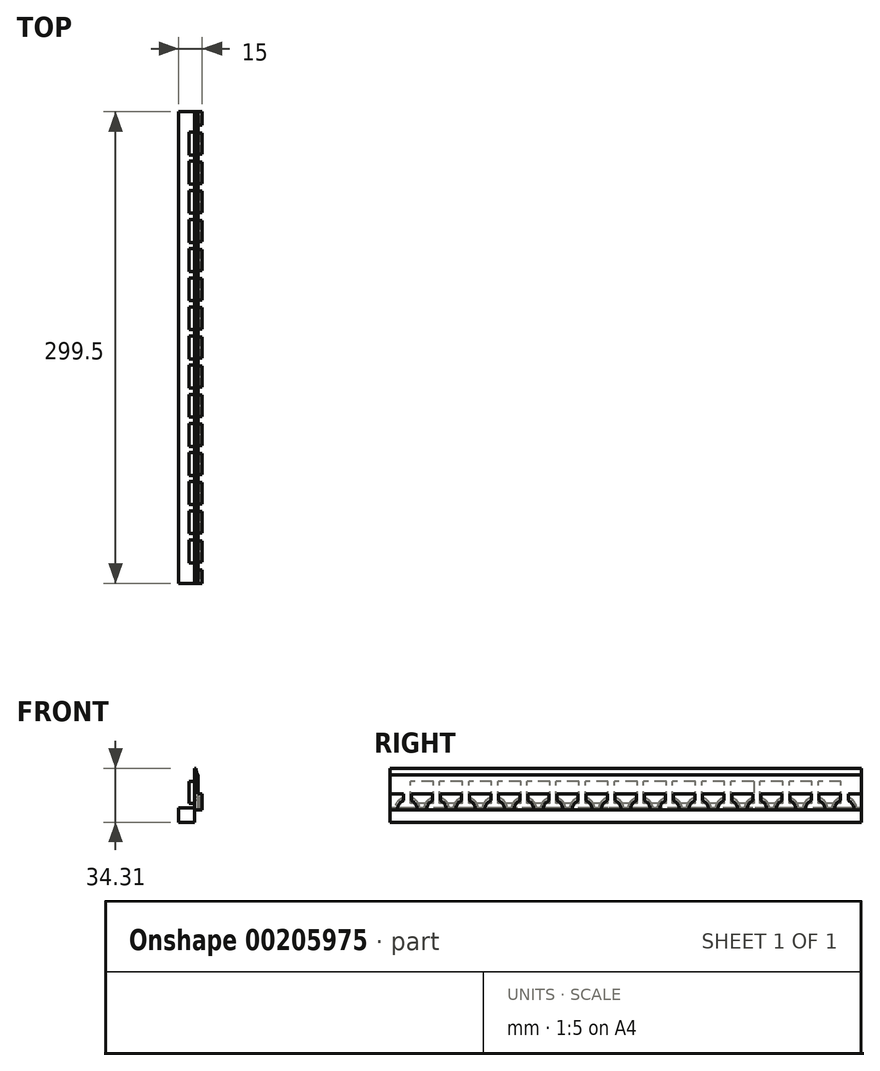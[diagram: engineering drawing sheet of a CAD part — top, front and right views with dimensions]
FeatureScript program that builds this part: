
annotation { "Feature Type Name" : "Feature", "Feature Type Description" : "" }
export const myFeature = defineFeature(function(context is Context, id is Id, definition is map)
    precondition{}
    {
        {
            var Q0;
            Q0=qCreatedBy(makeId("Front.planeOp"),FACE);
            var sketch = newSketch(context, id + "F0", { "sketchPlane" : qUnion([Q0])});
            skLineSegment(sketch, "E0.left", {"start": v(0, -1.35) * mm, "end": v(0, -9) * mm});
            skLineSegment(sketch, "E0.right", {"start": v(-10, 0) * mm, "end": v(-10, -9) * mm});
            skLineSegment(sketch, "E1.left", {"start": v(0, 1) * mm, "end": v(0, 4) * mm});
            skLineSegment(sketch, "E2", {"start": v(0, 21) * mm, "end": v(0, 25.3) * mm});
            skLineSegment(sketch, "E3", {"start": v(2.3, 21) * mm, "end": v(2.3, 10) * mm});
            skLineSegment(sketch, "E4", {"start": v(-10, -9) * mm, "end": v(0, -9) * mm});
            skLineSegment(sketch, "E5", {"start": v(0, 21) * mm, "end": v(0, 4) * mm});
            skLineSegment(sketch, "E6", {"start": v(2.3, 10) * mm, "end": v(2.3, 0) * mm});
            skLineSegment(sketch, "E7", {"start": v(2.3, 0) * mm, "end": v(2.3, -1) * mm});
            skLineSegment(sketch, "E8", {"start": v(-10, 0) * mm, "end": v(0, 0) * mm});
            skLineSegment(sketch, "E9", {"start": v(0, 25.3) * mm, "end": v(1, 25.3) * mm});
            skFitSpline(sketch, "E10", {"points": [v(1, 25.3) * mm, v(2.3, 21) * mm, v(6.9, 18.23) * mm], "startDerivative": vector(1.27, -9.9) * mm, "endDerivative": vector(10.4, -4.34) * mm});
            skPoint(sketch, "E11.0.internal.orphan", {"position": v(1, 26) * mm});
            skLineSegment(sketch, "E12", {"start": v(0, 0) * mm, "end": v(0, 1) * mm});
            skLineSegment(sketch, "E13", {"start": v(0, 0) * mm, "end": v(0, -1) * mm});
            skLineSegment(sketch, "E14", {"start": v(0, -1) * mm, "end": v(2.3, -1) * mm});
            skLineSegment(sketch, "E15", {"start": v(0, -1) * mm, "end": v(0, -1.35) * mm});
            skPoint(sketch, "E16.orphan", {"position": v(2.3, -1.35) * mm});
            skSolve(sketch);
        }
        {
            var Q0;
            Q0=qCreatedBy(makeId("Right.planeOp"),FACE);
            var sketch = newSketch(context, id + "F1", { "sketchPlane" : qUnion([Q0])});
            skLineSegment(sketch, "E17.left", {"start": v(13, 4) * mm, "end": v(13, 17) * mm});
            skLineSegment(sketch, "E17.right", {"start": v(27.5, 4) * mm, "end": v(27.5, 17) * mm});
            skLineSegment(sketch, "E18.left", {"start": v(31.5, 4) * mm, "end": v(31.5, 17) * mm});
            skLineSegment(sketch, "E18.right", {"start": v(46, 4) * mm, "end": v(46, 17) * mm});
            skLineSegment(sketch, "E19.left", {"start": v(50, 4) * mm, "end": v(50, 17) * mm});
            skLineSegment(sketch, "E19.right", {"start": v(64.5, 4) * mm, "end": v(64.5, 17) * mm});
            skLineSegment(sketch, "E20.left", {"start": v(68.5, 4) * mm, "end": v(68.5, 17) * mm});
            skLineSegment(sketch, "E20.right", {"start": v(83, 4) * mm, "end": v(83, 17) * mm});
            skLineSegment(sketch, "E21.left", {"start": v(87, 4) * mm, "end": v(87, 17) * mm});
            skLineSegment(sketch, "E21.right", {"start": v(101.5, 4) * mm, "end": v(101.5, 17) * mm});
            skLineSegment(sketch, "E22.left", {"start": v(105.5, 4) * mm, "end": v(105.5, 17) * mm});
            skLineSegment(sketch, "E22.right", {"start": v(120, 4) * mm, "end": v(120, 17) * mm});
            skLineSegment(sketch, "E23.left", {"start": v(124, 4) * mm, "end": v(124, 17) * mm});
            skLineSegment(sketch, "E23.right", {"start": v(138.5, 4) * mm, "end": v(138.5, 17) * mm});
            skLineSegment(sketch, "E24.left", {"start": v(142.5, 4) * mm, "end": v(142.5, 17) * mm});
            skLineSegment(sketch, "E24.right", {"start": v(157, 4) * mm, "end": v(157, 17) * mm});
            skLineSegment(sketch, "E25.left", {"start": v(161, 4) * mm, "end": v(161, 17) * mm});
            skLineSegment(sketch, "E25.right", {"start": v(175.5, 4) * mm, "end": v(175.5, 17) * mm});
            skLineSegment(sketch, "E26.left", {"start": v(179.5, 4) * mm, "end": v(179.5, 17) * mm});
            skLineSegment(sketch, "E26.right", {"start": v(194, 4) * mm, "end": v(194, 17) * mm});
            skLineSegment(sketch, "E27.left", {"start": v(198, 4) * mm, "end": v(198, 17) * mm});
            skLineSegment(sketch, "E27.right", {"start": v(212.5, 4) * mm, "end": v(212.5, 17) * mm});
            skLineSegment(sketch, "E28.left", {"start": v(216.5, 4) * mm, "end": v(216.5, 17) * mm});
            skLineSegment(sketch, "E28.right", {"start": v(231, 4) * mm, "end": v(231, 17) * mm});
            skLineSegment(sketch, "E29.left", {"start": v(235, 4) * mm, "end": v(235, 17) * mm});
            skLineSegment(sketch, "E29.right", {"start": v(249.5, 4) * mm, "end": v(249.5, 17) * mm});
            skLineSegment(sketch, "E30.left", {"start": v(253.5, 4) * mm, "end": v(253.5, 17) * mm});
            skLineSegment(sketch, "E30.right", {"start": v(268, 4) * mm, "end": v(268, 17) * mm});
            skLineSegment(sketch, "E31.left", {"start": v(272, 4) * mm, "end": v(272, 17) * mm});
            skLineSegment(sketch, "E31.right", {"start": v(286.5, 4) * mm, "end": v(286.5, 17) * mm});
            skLineSegment(sketch, "E32", {"start": v(286.5, 17) * mm, "end": v(272, 17) * mm});
            skLineSegment(sketch, "E33", {"start": v(286.5, 4) * mm, "end": v(286.5, 3) * mm});
            skLineSegment(sketch, "E34", {"start": v(286.5, 3) * mm, "end": v(272, 3) * mm});
            skLineSegment(sketch, "E35", {"start": v(13, 4) * mm, "end": v(13, 3) * mm});
            skLineSegment(sketch, "E36", {"start": v(27.5, 4) * mm, "end": v(27.5, 3) * mm});
            skLineSegment(sketch, "E37", {"start": v(31.5, 4) * mm, "end": v(31.5, 3) * mm});
            skLineSegment(sketch, "E38", {"start": v(46, 4) * mm, "end": v(46, 3) * mm});
            skLineSegment(sketch, "E39", {"start": v(50, 4) * mm, "end": v(50, 3) * mm});
            skLineSegment(sketch, "E40", {"start": v(64.5, 4) * mm, "end": v(64.5, 3) * mm});
            skLineSegment(sketch, "E41", {"start": v(68.5, 4) * mm, "end": v(68.5, 3) * mm});
            skLineSegment(sketch, "E42", {"start": v(83, 4) * mm, "end": v(83, 3) * mm});
            skLineSegment(sketch, "E43", {"start": v(87, 4) * mm, "end": v(87, 3) * mm});
            skLineSegment(sketch, "E44", {"start": v(101.5, 4) * mm, "end": v(101.5, 3) * mm});
            skLineSegment(sketch, "E45", {"start": v(105.5, 4) * mm, "end": v(105.5, 3) * mm});
            skLineSegment(sketch, "E46", {"start": v(120, 4) * mm, "end": v(120, 3) * mm});
            skLineSegment(sketch, "E47", {"start": v(124, 4) * mm, "end": v(124, 3) * mm});
            skLineSegment(sketch, "E48", {"start": v(138.5, 4) * mm, "end": v(138.5, 3) * mm});
            skLineSegment(sketch, "E49", {"start": v(142.5, 4) * mm, "end": v(142.5, 3) * mm});
            skLineSegment(sketch, "E50", {"start": v(157, 4) * mm, "end": v(157, 3) * mm});
            skLineSegment(sketch, "E51", {"start": v(161, 4) * mm, "end": v(161, 3) * mm});
            skLineSegment(sketch, "E52", {"start": v(175.5, 4) * mm, "end": v(175.5, 3) * mm});
            skLineSegment(sketch, "E53", {"start": v(179.5, 4) * mm, "end": v(179.5, 3) * mm});
            skLineSegment(sketch, "E54", {"start": v(194, 4) * mm, "end": v(194, 3) * mm});
            skLineSegment(sketch, "E55", {"start": v(198, 4) * mm, "end": v(198, 3) * mm});
            skLineSegment(sketch, "E56", {"start": v(212.5, 4) * mm, "end": v(212.5, 3) * mm});
            skLineSegment(sketch, "E57", {"start": v(216.5, 4) * mm, "end": v(216.5, 3) * mm});
            skLineSegment(sketch, "E58", {"start": v(231, 4) * mm, "end": v(231, 3) * mm});
            skLineSegment(sketch, "E59", {"start": v(235, 4) * mm, "end": v(235, 3) * mm});
            skLineSegment(sketch, "E60", {"start": v(249.5, 4) * mm, "end": v(249.5, 3) * mm});
            skLineSegment(sketch, "E61", {"start": v(253.5, 4) * mm, "end": v(253.5, 3) * mm});
            skLineSegment(sketch, "E62", {"start": v(268, 4) * mm, "end": v(268, 3) * mm});
            skLineSegment(sketch, "E63", {"start": v(272, 4) * mm, "end": v(272, 3) * mm});
            skLineSegment(sketch, "E64.trimOffspring", {"start": v(268, 17) * mm, "end": v(253.5, 17) * mm});
            skLineSegment(sketch, "E65.trimOffspring", {"start": v(249.5, 17) * mm, "end": v(235, 17) * mm});
            skLineSegment(sketch, "E66.trimOffspring", {"start": v(268, 3) * mm, "end": v(253.5, 3) * mm});
            skLineSegment(sketch, "E67.trimOffspring", {"start": v(249.5, 3) * mm, "end": v(235, 3) * mm});
            skLineSegment(sketch, "E68.trimOffspring", {"start": v(231, 3) * mm, "end": v(216.5, 3) * mm});
            skLineSegment(sketch, "E69.trimOffspring", {"start": v(231, 17) * mm, "end": v(216.5, 17) * mm});
            skLineSegment(sketch, "E70.trimOffspring", {"start": v(212.5, 17) * mm, "end": v(198, 17) * mm});
            skLineSegment(sketch, "E71.trimOffspring", {"start": v(212.5, 3) * mm, "end": v(198, 3) * mm});
            skLineSegment(sketch, "E72.trimOffspring", {"start": v(194, 17) * mm, "end": v(179.5, 17) * mm});
            skLineSegment(sketch, "E73.trimOffspring", {"start": v(194, 3) * mm, "end": v(179.5, 3) * mm});
            skLineSegment(sketch, "E74.trimOffspring", {"start": v(175.5, 17) * mm, "end": v(161, 17) * mm});
            skLineSegment(sketch, "E75.trimOffspring", {"start": v(175.5, 3) * mm, "end": v(161, 3) * mm});
            skLineSegment(sketch, "E76.trimOffspring", {"start": v(157, 17) * mm, "end": v(142.5, 17) * mm});
            skLineSegment(sketch, "E77.trimOffspring", {"start": v(157, 3) * mm, "end": v(142.5, 3) * mm});
            skLineSegment(sketch, "E78.trimOffspring", {"start": v(138.5, 17) * mm, "end": v(124, 17) * mm});
            skLineSegment(sketch, "E79.trimOffspring", {"start": v(138.5, 3) * mm, "end": v(124, 3) * mm});
            skLineSegment(sketch, "E80.trimOffspring", {"start": v(120, 17) * mm, "end": v(105.5, 17) * mm});
            skLineSegment(sketch, "E81.trimOffspring", {"start": v(120, 3) * mm, "end": v(105.5, 3) * mm});
            skLineSegment(sketch, "E82.trimOffspring", {"start": v(101.5, 17) * mm, "end": v(87, 17) * mm});
            skLineSegment(sketch, "E83.trimOffspring", {"start": v(101.5, 3) * mm, "end": v(87, 3) * mm});
            skLineSegment(sketch, "E84.trimOffspring", {"start": v(83, 17) * mm, "end": v(68.5, 17) * mm});
            skLineSegment(sketch, "E85.trimOffspring", {"start": v(83, 3) * mm, "end": v(68.5, 3) * mm});
            skLineSegment(sketch, "E86.trimOffspring", {"start": v(64.5, 17) * mm, "end": v(50, 17) * mm});
            skLineSegment(sketch, "E87.trimOffspring", {"start": v(64.5, 3) * mm, "end": v(50, 3) * mm});
            skLineSegment(sketch, "E88.trimOffspring", {"start": v(46, 17) * mm, "end": v(31.5, 17) * mm});
            skLineSegment(sketch, "E89.trimOffspring", {"start": v(46, 3) * mm, "end": v(31.5, 3) * mm});
            skLineSegment(sketch, "E90.trimOffspring", {"start": v(27.5, 17) * mm, "end": v(13, 17) * mm});
            skLineSegment(sketch, "E91.trimOffspring", {"start": v(27.5, 3) * mm, "end": v(13, 3) * mm});
            skPoint(sketch, "E92.orphan", {"position": v(13, 18) * mm});
            skSolve(sketch);
        }
        {
            var Q0;
            Q0=qCreatedBy(makeId("Right.planeOp"),FACE);
            var sketch = newSketch(context, id + "F2", { "sketchPlane" : qUnion([Q0])});
            skLineSegment(sketch, "E93", {"start": v(0, 0) * mm, "end": v(0, -1) * mm});
            skLineSegment(sketch, "E94.bottom", {"start": v(0, -1) * mm, "end": v(4.75, -1) * mm});
            skLineSegment(sketch, "E95.top", {"start": v(0, 9) * mm, "end": v(8.5, 9) * mm});
            skLineSegment(sketch, "E95.left", {"start": v(0, -1) * mm, "end": v(0, 9) * mm});
            skLineSegment(sketch, "E95.right", {"start": v(8.5, 4.73) * mm, "end": v(8.5, 9) * mm});
            skLineSegment(sketch, "E96.bottom", {"start": v(17.25, -1) * mm, "end": v(23.25, -1) * mm});
            skLineSegment(sketch, "E96.top", {"start": v(13.5, 9) * mm, "end": v(27, 9) * mm});
            skLineSegment(sketch, "E96.left", {"start": v(13.5, 4.73) * mm, "end": v(13.5, 9) * mm});
            skLineSegment(sketch, "E96.right", {"start": v(27, 4.73) * mm, "end": v(27, 9) * mm});
            skArc(sketch, "E97", {"start": v(19.05, -1) * mm, "mid": v(17.52, 3.73) * mm, "end": v(13.5, 6.65) * mm});
            skArc(sketch, "E98", {"start": v(17.25, -1) * mm, "mid": v(16.23, 2.42) * mm, "end": v(13.5, 4.73) * mm});
            skLineSegment(sketch, "E99", {"start": v(35.75, -1) * mm, "end": v(41.75, -1) * mm});
            skLineSegment(sketch, "E100", {"start": v(54.25, -1) * mm, "end": v(60.25, -1) * mm});
            skLineSegment(sketch, "E101", {"start": v(72.75, -1) * mm, "end": v(78.75, -1) * mm});
            skLineSegment(sketch, "E102", {"start": v(91.25, -1) * mm, "end": v(97.25, -1) * mm});
            skLineSegment(sketch, "E103", {"start": v(109.75, -1) * mm, "end": v(115.75, -1) * mm});
            skLineSegment(sketch, "E104", {"start": v(130.1, -1) * mm, "end": v(134.25, -1) * mm});
            skLineSegment(sketch, "E105", {"start": v(146.75, -1) * mm, "end": v(152.75, -1) * mm});
            skLineSegment(sketch, "E106", {"start": v(165.25, -1) * mm, "end": v(169.4, -1) * mm});
            skLineSegment(sketch, "E107", {"start": v(180, -1) * mm, "end": v(189.75, -1) * mm});
            skLineSegment(sketch, "E108", {"start": v(202.25, -1) * mm, "end": v(208.25, -1) * mm});
            skLineSegment(sketch, "E109", {"start": v(222.6, -1) * mm, "end": v(226.75, -1) * mm});
            skLineSegment(sketch, "E110", {"start": v(239.25, -1) * mm, "end": v(245.25, -1) * mm});
            skLineSegment(sketch, "E111", {"start": v(257.75, -1) * mm, "end": v(263.75, -1) * mm});
            skPoint(sketch, "E112.endSnap0", {"position": v(168.25, -1) * mm});
            skLineSegment(sketch, "E113", {"start": v(276.25, -1) * mm, "end": v(282.25, -1) * mm});
            skLineSegment(sketch, "E114", {"start": v(294.75, -1) * mm, "end": v(299.5, -1) * mm});
            skArc(sketch, "E115", {"start": v(286, 6.7) * mm, "mid": v(281.95, 3.76) * mm, "end": v(280.4, -1) * mm});
            skArc(sketch, "E116", {"start": v(294.75, -1) * mm, "mid": v(293.73, 2.42) * mm, "end": v(291, 4.72) * mm});
            skArc(sketch, "E117", {"start": v(278.1, -1) * mm, "mid": v(276.55, 3.76) * mm, "end": v(272.5, 6.7) * mm});
            skArc(sketch, "E118", {"start": v(276.25, -1) * mm, "mid": v(275.23, 2.42) * mm, "end": v(272.5, 4.72) * mm});
            skArc(sketch, "E119", {"start": v(259.6, -1) * mm, "mid": v(258.05, 3.76) * mm, "end": v(254, 6.7) * mm});
            skArc(sketch, "E120", {"start": v(257.75, -1) * mm, "mid": v(256.73, 2.42) * mm, "end": v(254, 4.72) * mm});
            skArc(sketch, "E121", {"start": v(241.1, -1) * mm, "mid": v(239.55, 3.76) * mm, "end": v(235.5, 6.7) * mm});
            skArc(sketch, "E122", {"start": v(239.25, -1) * mm, "mid": v(238.23, 2.42) * mm, "end": v(235.5, 4.72) * mm});
            skArc(sketch, "E123", {"start": v(222.6, -1) * mm, "mid": v(221.05, 3.76) * mm, "end": v(217, 6.7) * mm});
            skArc(sketch, "E124", {"start": v(220.75, -1) * mm, "mid": v(219.73, 2.42) * mm, "end": v(217, 4.72) * mm});
            skArc(sketch, "E125", {"start": v(204.1, -1) * mm, "mid": v(202.55, 3.76) * mm, "end": v(198.5, 6.7) * mm});
            skArc(sketch, "E126", {"start": v(202.25, -1) * mm, "mid": v(201.23, 2.42) * mm, "end": v(198.5, 4.72) * mm});
            skArc(sketch, "E127", {"start": v(185.6, -1) * mm, "mid": v(184.05, 3.76) * mm, "end": v(180, 6.7) * mm});
            skArc(sketch, "E128", {"start": v(183.75, -1) * mm, "mid": v(182.73, 2.42) * mm, "end": v(180, 4.72) * mm});
            skArc(sketch, "E129", {"start": v(167.1, -1) * mm, "mid": v(165.55, 3.76) * mm, "end": v(161.5, 6.7) * mm});
            skArc(sketch, "E130", {"start": v(165.25, -1) * mm, "mid": v(164.23, 2.42) * mm, "end": v(161.5, 4.72) * mm});
            skArc(sketch, "E131", {"start": v(148.6, -1) * mm, "mid": v(147.05, 3.76) * mm, "end": v(143, 6.7) * mm});
            skArc(sketch, "E132", {"start": v(146.75, -1) * mm, "mid": v(145.73, 2.42) * mm, "end": v(143, 4.72) * mm});
            skArc(sketch, "E133", {"start": v(130.1, -1) * mm, "mid": v(128.55, 3.76) * mm, "end": v(124.5, 6.7) * mm});
            skArc(sketch, "E134", {"start": v(128.25, -1) * mm, "mid": v(127.23, 2.42) * mm, "end": v(124.5, 4.72) * mm});
            skArc(sketch, "E135", {"start": v(111.6, -1) * mm, "mid": v(110.05, 3.76) * mm, "end": v(106, 6.7) * mm});
            skArc(sketch, "E136", {"start": v(109.75, -1) * mm, "mid": v(108.73, 2.42) * mm, "end": v(106, 4.72) * mm});
            skArc(sketch, "E137", {"start": v(93.1, -1) * mm, "mid": v(91.55, 3.76) * mm, "end": v(87.5, 6.7) * mm});
            skArc(sketch, "E138", {"start": v(91.25, -1) * mm, "mid": v(90.23, 2.42) * mm, "end": v(87.5, 4.73) * mm});
            skArc(sketch, "E139", {"start": v(74.6, -1) * mm, "mid": v(73.05, 3.76) * mm, "end": v(69, 6.7) * mm});
            skArc(sketch, "E140", {"start": v(72.75, -1) * mm, "mid": v(71.73, 2.42) * mm, "end": v(69, 4.73) * mm});
            skArc(sketch, "E141", {"start": v(56.1, -1) * mm, "mid": v(54.55, 3.76) * mm, "end": v(50.5, 6.7) * mm});
            skArc(sketch, "E142", {"start": v(54.25, -1) * mm, "mid": v(53.23, 2.42) * mm, "end": v(50.5, 4.73) * mm});
            skArc(sketch, "E143", {"start": v(37.6, -1) * mm, "mid": v(36.05, 3.76) * mm, "end": v(32, 6.7) * mm});
            skArc(sketch, "E144", {"start": v(35.75, -1) * mm, "mid": v(34.73, 2.42) * mm, "end": v(32, 4.73) * mm});
            skLineSegment(sketch, "E145.top", {"start": v(32, 9) * mm, "end": v(45.5, 9) * mm});
            skLineSegment(sketch, "E145.left", {"start": v(32, 4.73) * mm, "end": v(32, 9) * mm});
            skLineSegment(sketch, "E145.right", {"start": v(45.5, 4.73) * mm, "end": v(45.5, 9) * mm});
            skLineSegment(sketch, "E146.bottom", {"start": v(60.25, -1) * mm, "end": v(54.25, -1) * mm});
            skLineSegment(sketch, "E146.top", {"start": v(64, 9) * mm, "end": v(50.5, 9) * mm});
            skLineSegment(sketch, "E146.left", {"start": v(64, 4.73) * mm, "end": v(64, 9) * mm});
            skLineSegment(sketch, "E146.right", {"start": v(50.5, 4.73) * mm, "end": v(50.5, 9) * mm});
            skLineSegment(sketch, "E147.bottom", {"start": v(72.75, -1) * mm, "end": v(76.9, -1) * mm});
            skLineSegment(sketch, "E147.top", {"start": v(69, 9) * mm, "end": v(82.5, 9) * mm});
            skLineSegment(sketch, "E147.left", {"start": v(69, 4.73) * mm, "end": v(69, 9) * mm});
            skLineSegment(sketch, "E147.right", {"start": v(82.5, 4.73) * mm, "end": v(82.5, 9) * mm});
            skLineSegment(sketch, "E148.bottom", {"start": v(93.1, -1) * mm, "end": v(95.4, -1) * mm});
            skLineSegment(sketch, "E148.top", {"start": v(87.5, 9) * mm, "end": v(101, 9) * mm});
            skLineSegment(sketch, "E148.left", {"start": v(87.5, 4.73) * mm, "end": v(87.5, 9) * mm});
            skLineSegment(sketch, "E148.right", {"start": v(101, 4.72) * mm, "end": v(101, 9) * mm});
            skLineSegment(sketch, "E149.top", {"start": v(106, 9) * mm, "end": v(119.5, 9) * mm});
            skLineSegment(sketch, "E149.left", {"start": v(106, 4.72) * mm, "end": v(106, 9) * mm});
            skLineSegment(sketch, "E149.right", {"start": v(119.5, 4.72) * mm, "end": v(119.5, 9) * mm});
            skLineSegment(sketch, "E150.bottom", {"start": v(128.25, -1) * mm, "end": v(134.25, -1) * mm});
            skLineSegment(sketch, "E150.top", {"start": v(124.5, 9) * mm, "end": v(138, 9) * mm});
            skLineSegment(sketch, "E150.left", {"start": v(124.5, 4.72) * mm, "end": v(124.5, 9) * mm});
            skLineSegment(sketch, "E150.right", {"start": v(138, 4.72) * mm, "end": v(138, 9) * mm});
            skLineSegment(sketch, "E151.top", {"start": v(143, 9) * mm, "end": v(156.5, 9) * mm});
            skLineSegment(sketch, "E151.left", {"start": v(143, 4.72) * mm, "end": v(143, 9) * mm});
            skLineSegment(sketch, "E151.right", {"start": v(156.5, 4.72) * mm, "end": v(156.5, 9) * mm});
            skLineSegment(sketch, "E152.bottom", {"start": v(165.25, -1) * mm, "end": v(171.25, -1) * mm});
            skLineSegment(sketch, "E152.top", {"start": v(161.5, 9) * mm, "end": v(175, 9) * mm});
            skLineSegment(sketch, "E152.left", {"start": v(161.5, 4.72) * mm, "end": v(161.5, 9) * mm});
            skLineSegment(sketch, "E152.right", {"start": v(175, 4.72) * mm, "end": v(175, 9) * mm});
            skLineSegment(sketch, "E153.bottom", {"start": v(183.75, -1) * mm, "end": v(187.9, -1) * mm});
            skLineSegment(sketch, "E153.top", {"start": v(180, 9) * mm, "end": v(193.5, 9) * mm});
            skLineSegment(sketch, "E153.left", {"start": v(180, 4.72) * mm, "end": v(180, 9) * mm});
            skLineSegment(sketch, "E153.right", {"start": v(193.5, 4.72) * mm, "end": v(193.5, 9) * mm});
            skLineSegment(sketch, "E154.top", {"start": v(198.5, 9) * mm, "end": v(212, 9) * mm});
            skLineSegment(sketch, "E154.left", {"start": v(198.5, 4.72) * mm, "end": v(198.5, 9) * mm});
            skLineSegment(sketch, "E154.right", {"start": v(212, 4.72) * mm, "end": v(212, 9) * mm});
            skLineSegment(sketch, "E155.bottom", {"start": v(220.75, -1) * mm, "end": v(226.75, -1) * mm});
            skLineSegment(sketch, "E155.top", {"start": v(217, 9) * mm, "end": v(230.5, 9) * mm});
            skLineSegment(sketch, "E155.left", {"start": v(217, 4.72) * mm, "end": v(217, 9) * mm});
            skLineSegment(sketch, "E155.right", {"start": v(230.5, 4.72) * mm, "end": v(230.5, 9) * mm});
            skLineSegment(sketch, "E156.top", {"start": v(235.5, 9) * mm, "end": v(249, 9) * mm});
            skLineSegment(sketch, "E156.left", {"start": v(235.5, 4.72) * mm, "end": v(235.5, 9) * mm});
            skLineSegment(sketch, "E156.right", {"start": v(249, 4.72) * mm, "end": v(249, 9) * mm});
            skLineSegment(sketch, "E157.top", {"start": v(254, 9) * mm, "end": v(267.5, 9) * mm});
            skLineSegment(sketch, "E157.left", {"start": v(254, 4.72) * mm, "end": v(254, 9) * mm});
            skLineSegment(sketch, "E157.right", {"start": v(267.5, 4.72) * mm, "end": v(267.5, 9) * mm});
            skLineSegment(sketch, "E158.top", {"start": v(272.5, 9) * mm, "end": v(286, 9) * mm});
            skLineSegment(sketch, "E158.left", {"start": v(272.5, 4.72) * mm, "end": v(272.5, 9) * mm});
            skLineSegment(sketch, "E158.right", {"start": v(286, 4.72) * mm, "end": v(286, 9) * mm});
            skLineSegment(sketch, "E159.top", {"start": v(291, 9) * mm, "end": v(299.5, 9) * mm});
            skLineSegment(sketch, "E159.left", {"start": v(291, 4.72) * mm, "end": v(291, 9) * mm});
            skLineSegment(sketch, "E159.right", {"start": v(299.5, -1) * mm, "end": v(299.5, 9) * mm});
            skArc(sketch, "E160.trimOffspring", {"start": v(296.6, -1) * mm, "mid": v(295.05, 3.76) * mm, "end": v(291, 6.7) * mm});
            skArc(sketch, "E161.trimOffspring", {"start": v(286, 4.72) * mm, "mid": v(283.27, 2.42) * mm, "end": v(282.25, -1) * mm});
            skArc(sketch, "E162.trimOffspring", {"start": v(267.5, 6.7) * mm, "mid": v(263.45, 3.76) * mm, "end": v(261.9, -1) * mm});
            skArc(sketch, "E163.trimOffspring", {"start": v(249, 6.7) * mm, "mid": v(244.95, 3.76) * mm, "end": v(243.4, -1) * mm});
            skArc(sketch, "E164.trimOffspring", {"start": v(249, 4.72) * mm, "mid": v(246.27, 2.42) * mm, "end": v(245.25, -1) * mm});
            skArc(sketch, "E165.trimOffspring", {"start": v(267.5, 4.72) * mm, "mid": v(264.77, 2.42) * mm, "end": v(263.75, -1) * mm});
            skArc(sketch, "E166.trimOffspring", {"start": v(230.5, 4.72) * mm, "mid": v(227.77, 2.42) * mm, "end": v(226.75, -1) * mm});
            skArc(sketch, "E167.trimOffspring", {"start": v(230.5, 6.7) * mm, "mid": v(226.45, 3.76) * mm, "end": v(224.9, -1) * mm});
            skArc(sketch, "E168.trimOffspring", {"start": v(212, 4.72) * mm, "mid": v(209.27, 2.42) * mm, "end": v(208.25, -1) * mm});
            skArc(sketch, "E169.trimOffspring", {"start": v(212, 6.7) * mm, "mid": v(207.95, 3.76) * mm, "end": v(206.4, -1) * mm});
            skArc(sketch, "E170.trimOffspring", {"start": v(193.5, 4.72) * mm, "mid": v(190.77, 2.42) * mm, "end": v(189.75, -1) * mm});
            skArc(sketch, "E171.trimOffspring", {"start": v(193.5, 6.7) * mm, "mid": v(189.45, 3.76) * mm, "end": v(187.9, -1) * mm});
            skArc(sketch, "E172.trimOffspring", {"start": v(175, 6.7) * mm, "mid": v(170.95, 3.76) * mm, "end": v(169.4, -1) * mm});
            skArc(sketch, "E173.trimOffspring", {"start": v(175, 4.72) * mm, "mid": v(172.27, 2.42) * mm, "end": v(171.25, -1) * mm});
            skPoint(sketch, "E174.orphan", {"position": v(175, -1) * mm});
            skPoint(sketch, "E175.orphan", {"position": v(161.5, -1) * mm});
            skArc(sketch, "E176.trimOffspring", {"start": v(156.5, 4.72) * mm, "mid": v(153.77, 2.42) * mm, "end": v(152.75, -1) * mm});
            skArc(sketch, "E177.trimOffspring", {"start": v(156.5, 6.7) * mm, "mid": v(152.45, 3.76) * mm, "end": v(150.9, -1) * mm});
            skArc(sketch, "E178.trimOffspring", {"start": v(138, 6.7) * mm, "mid": v(133.95, 3.76) * mm, "end": v(132.4, -1) * mm});
            skArc(sketch, "E179.trimOffspring", {"start": v(138, 4.72) * mm, "mid": v(135.27, 2.42) * mm, "end": v(134.25, -1) * mm});
            skArc(sketch, "E180.trimOffspring", {"start": v(119.5, 6.7) * mm, "mid": v(115.45, 3.76) * mm, "end": v(113.9, -1) * mm});
            skArc(sketch, "E181.trimOffspring", {"start": v(119.5, 4.72) * mm, "mid": v(116.77, 2.42) * mm, "end": v(115.75, -1) * mm});
            skArc(sketch, "E182.trimOffspring", {"start": v(101, 4.72) * mm, "mid": v(98.27, 2.42) * mm, "end": v(97.25, -1) * mm});
            skArc(sketch, "E183.trimOffspring", {"start": v(101, 6.7) * mm, "mid": v(96.95, 3.76) * mm, "end": v(95.4, -1) * mm});
            skArc(sketch, "E184.trimOffspring", {"start": v(82.5, 6.7) * mm, "mid": v(78.45, 3.76) * mm, "end": v(76.9, -1) * mm});
            skArc(sketch, "E185.trimOffspring", {"start": v(82.5, 4.73) * mm, "mid": v(79.77, 2.42) * mm, "end": v(78.75, -1) * mm});
            skArc(sketch, "E186.trimOffspring", {"start": v(64, 4.73) * mm, "mid": v(61.27, 2.42) * mm, "end": v(60.25, -1) * mm});
            skArc(sketch, "E187.trimOffspring", {"start": v(64, 6.7) * mm, "mid": v(59.95, 3.76) * mm, "end": v(58.4, -1) * mm});
            skArc(sketch, "E188.trimOffspring", {"start": v(45.5, 6.7) * mm, "mid": v(41.45, 3.76) * mm, "end": v(39.9, -1) * mm});
            skArc(sketch, "E189.trimOffspring", {"start": v(45.5, 4.73) * mm, "mid": v(42.77, 2.42) * mm, "end": v(41.75, -1) * mm});
            skArc(sketch, "E190.trimOffspring", {"start": v(27, 4.73) * mm, "mid": v(24.27, 2.42) * mm, "end": v(23.25, -1) * mm});
            skArc(sketch, "E191.trimOffspring", {"start": v(27, 6.7) * mm, "mid": v(22.95, 3.76) * mm, "end": v(21.4, -1) * mm});
            skArc(sketch, "E192.trimOffspring", {"start": v(8.5, 6.65) * mm, "mid": v(4.48, 3.73) * mm, "end": v(2.95, -1) * mm});
            skArc(sketch, "E193.trimOffspring", {"start": v(8.5, 4.73) * mm, "mid": v(5.77, 2.42) * mm, "end": v(4.75, -1) * mm});
            skPoint(sketch, "E194.orphan", {"position": v(13.5, -1) * mm});
            skPoint(sketch, "E195.orphan", {"position": v(8.5, -1) * mm});
            skSolve(sketch);
        }
        {
            var Q0;
            Q0 = qSketchRegion(id + "F0", true);
            extrude(context, id + "F3", {"entities" : qUnion([Q0]), "oppositeDirection" : true, "depth" : 299.5 * mm});
        }
        {
            var Q0;
            Q0 = qSketchRegion(id + "F1", true);
            extrude(context, id + "F4", {"entities" : qUnion([Q0]), "operationType" : NewBodyOperationType.ADD, "oppositeDirection" : true, "depth" : 3.5 * mm});
        }
        {
            var Q0;
            Q0 = qSketchRegion(id + "F2", true);
            extrude(context, id + "F5", {"entities" : qUnion([Q0]), "operationType" : NewBodyOperationType.ADD, "depth" : 5 * mm});
        }
        {
            var Q0;
            {var subQ2=sQuery(id+"F2.wireOp",EDGE,"E192.trimOffspring");Q0=makeQuery(id+"F2.imprint","IMPRINT",FACE,{"disambiguationData":[TD([[makeQuery(id+"F2.imprint","IMPRINT",EDGE,{"derivedFrom":subQ2}),1.0]])]});}
            var Q1;
            {var subQ2=sQuery(id+"F2.wireOp",EDGE,"E97");Q1=makeQuery(id+"F2.imprint","IMPRINT",FACE,{"disambiguationData":[TD([[makeQuery(id+"F2.imprint","IMPRINT",EDGE,{"derivedFrom":subQ2}),1.0]])]});}
            var Q2;
            {var subQ0=sQuery(id+"F2.wireOp",EDGE,"E190.trimOffspring");Q2=makeQuery(id+"F2.imprint","IMPRINT",FACE,{"disambiguationData":[TD([[makeQuery(id+"F2.imprint","IMPRINT",EDGE,{"derivedFrom":subQ0}),-1.0]])]});}
            var Q3;
            Q3=makeQuery(id+"F2.imprint","IMPRINT",FACE,{"disambiguationData":[TD([[makeQuery(id+"F2.imprint","IMPRINT",EDGE,{"derivedFrom":sQuery(id+"F2.wireOp",EDGE,"E101")}),1.0]])]});
            var Q4;
            {var subQ2=sQuery(id+"F2.wireOp",EDGE,"E137");Q4=makeQuery(id+"F2.imprint","IMPRINT",FACE,{"disambiguationData":[TD([[makeQuery(id+"F2.imprint","IMPRINT",EDGE,{"derivedFrom":subQ2}),1.0]])]});}
            var Q5;
            {var subQ0=sQuery(id+"F2.wireOp",EDGE,"E182.trimOffspring");Q5=makeQuery(id+"F2.imprint","IMPRINT",FACE,{"disambiguationData":[TD([[makeQuery(id+"F2.imprint","IMPRINT",EDGE,{"derivedFrom":subQ0}),-1.0]])]});}
            var Q6;
            {var subQ0=sQuery(id+"F2.wireOp",EDGE,"E170.trimOffspring");Q6=makeQuery(id+"F2.imprint","IMPRINT",FACE,{"disambiguationData":[TD([[makeQuery(id+"F2.imprint","IMPRINT",EDGE,{"derivedFrom":subQ0}),-1.0]])]});}
            var Q7;
            {var subQ0=sQuery(id+"F2.wireOp",EDGE,"E115");Q7=makeQuery(id+"F2.imprint","IMPRINT",FACE,{"disambiguationData":[TD([[makeQuery(id+"F2.imprint","IMPRINT",EDGE,{"derivedFrom":subQ0}),1.0]])]});}
            var Q8;
            {var subQ0=sQuery(id+"F2.wireOp",EDGE,"E116");Q8=makeQuery(id+"F2.imprint","IMPRINT",FACE,{"disambiguationData":[TD([[makeQuery(id+"F2.imprint","IMPRINT",EDGE,{"derivedFrom":subQ0}),-1.0]])]});}
            var Q9;
            {var subQ0=sQuery(id+"F2.wireOp",EDGE,"E117");Q9=makeQuery(id+"F2.imprint","IMPRINT",FACE,{"disambiguationData":[TD([[makeQuery(id+"F2.imprint","IMPRINT",EDGE,{"derivedFrom":subQ0}),1.0]])]});}
            var Q10;
            {var subQ0=sQuery(id+"F2.wireOp",EDGE,"E119");Q10=makeQuery(id+"F2.imprint","IMPRINT",FACE,{"disambiguationData":[TD([[makeQuery(id+"F2.imprint","IMPRINT",EDGE,{"derivedFrom":subQ0}),1.0]])]});}
            var Q11;
            {var subQ0=sQuery(id+"F2.wireOp",EDGE,"E121");Q11=makeQuery(id+"F2.imprint","IMPRINT",FACE,{"disambiguationData":[TD([[makeQuery(id+"F2.imprint","IMPRINT",EDGE,{"derivedFrom":subQ0}),1.0]])]});}
            var Q12;
            {var subQ0=sQuery(id+"F2.wireOp",EDGE,"E123");Q12=makeQuery(id+"F2.imprint","IMPRINT",FACE,{"disambiguationData":[TD([[makeQuery(id+"F2.imprint","IMPRINT",EDGE,{"derivedFrom":subQ0}),1.0]])]});}
            var Q13;
            {var subQ0=sQuery(id+"F2.wireOp",EDGE,"E125");Q13=makeQuery(id+"F2.imprint","IMPRINT",FACE,{"disambiguationData":[TD([[makeQuery(id+"F2.imprint","IMPRINT",EDGE,{"derivedFrom":subQ0}),1.0]])]});}
            var Q14;
            {var subQ0=sQuery(id+"F2.wireOp",EDGE,"E127");Q14=makeQuery(id+"F2.imprint","IMPRINT",FACE,{"disambiguationData":[TD([[makeQuery(id+"F2.imprint","IMPRINT",EDGE,{"derivedFrom":subQ0}),1.0]])]});}
            var Q15;
            {var subQ0=sQuery(id+"F2.wireOp",EDGE,"E129");Q15=makeQuery(id+"F2.imprint","IMPRINT",FACE,{"disambiguationData":[TD([[makeQuery(id+"F2.imprint","IMPRINT",EDGE,{"derivedFrom":subQ0}),1.0]])]});}
            var Q16;
            {var subQ0=sQuery(id+"F2.wireOp",EDGE,"E131");Q16=makeQuery(id+"F2.imprint","IMPRINT",FACE,{"disambiguationData":[TD([[makeQuery(id+"F2.imprint","IMPRINT",EDGE,{"derivedFrom":subQ0}),1.0]])]});}
            var Q17;
            {var subQ0=sQuery(id+"F2.wireOp",EDGE,"E133");Q17=makeQuery(id+"F2.imprint","IMPRINT",FACE,{"disambiguationData":[TD([[makeQuery(id+"F2.imprint","IMPRINT",EDGE,{"derivedFrom":subQ0}),1.0]])]});}
            var Q18;
            {var subQ0=sQuery(id+"F2.wireOp",EDGE,"E135");Q18=makeQuery(id+"F2.imprint","IMPRINT",FACE,{"disambiguationData":[TD([[makeQuery(id+"F2.imprint","IMPRINT",EDGE,{"derivedFrom":subQ0}),1.0]])]});}
            var Q19;
            {var subQ0=sQuery(id+"F2.wireOp",EDGE,"E139");Q19=makeQuery(id+"F2.imprint","IMPRINT",FACE,{"disambiguationData":[TD([[makeQuery(id+"F2.imprint","IMPRINT",EDGE,{"derivedFrom":subQ0}),1.0]])]});}
            var Q20;
            {var subQ0=sQuery(id+"F2.wireOp",EDGE,"E141");Q20=makeQuery(id+"F2.imprint","IMPRINT",FACE,{"disambiguationData":[TD([[makeQuery(id+"F2.imprint","IMPRINT",EDGE,{"derivedFrom":subQ0}),1.0]])]});}
            var Q21;
            {var subQ0=sQuery(id+"F2.wireOp",EDGE,"E143");Q21=makeQuery(id+"F2.imprint","IMPRINT",FACE,{"disambiguationData":[TD([[makeQuery(id+"F2.imprint","IMPRINT",EDGE,{"derivedFrom":subQ0}),1.0]])]});}
            var Q22;
            {var subQ2=sQuery(id+"F2.wireOp",EDGE,"E188.trimOffspring");Q22=makeQuery(id+"F2.imprint","IMPRINT",FACE,{"disambiguationData":[TD([[makeQuery(id+"F2.imprint","IMPRINT",EDGE,{"derivedFrom":subQ2}),1.0]])]});}
            var Q23;
            {var subQ0=sQuery(id+"F2.wireOp",EDGE,"E186.trimOffspring");Q23=makeQuery(id+"F2.imprint","IMPRINT",FACE,{"disambiguationData":[TD([[makeQuery(id+"F2.imprint","IMPRINT",EDGE,{"derivedFrom":subQ0}),-1.0]])]});}
            var Q24;
            {var subQ2=sQuery(id+"F2.wireOp",EDGE,"E180.trimOffspring");Q24=makeQuery(id+"F2.imprint","IMPRINT",FACE,{"disambiguationData":[TD([[makeQuery(id+"F2.imprint","IMPRINT",EDGE,{"derivedFrom":subQ2}),1.0]])]});}
            var Q25;
            {var subQ2=sQuery(id+"F2.wireOp",EDGE,"E178.trimOffspring");Q25=makeQuery(id+"F2.imprint","IMPRINT",FACE,{"disambiguationData":[TD([[makeQuery(id+"F2.imprint","IMPRINT",EDGE,{"derivedFrom":subQ2}),1.0]])]});}
            var Q26;
            {var subQ0=sQuery(id+"F2.wireOp",EDGE,"E176.trimOffspring");Q26=makeQuery(id+"F2.imprint","IMPRINT",FACE,{"disambiguationData":[TD([[makeQuery(id+"F2.imprint","IMPRINT",EDGE,{"derivedFrom":subQ0}),-1.0]])]});}
            var Q27;
            {var subQ2=sQuery(id+"F2.wireOp",EDGE,"E172.trimOffspring");Q27=makeQuery(id+"F2.imprint","IMPRINT",FACE,{"disambiguationData":[TD([[makeQuery(id+"F2.imprint","IMPRINT",EDGE,{"derivedFrom":subQ2}),1.0]])]});}
            var Q28;
            {var subQ0=sQuery(id+"F2.wireOp",EDGE,"E168.trimOffspring");Q28=makeQuery(id+"F2.imprint","IMPRINT",FACE,{"disambiguationData":[TD([[makeQuery(id+"F2.imprint","IMPRINT",EDGE,{"derivedFrom":subQ0}),-1.0]])]});}
            var Q29;
            {var subQ0=sQuery(id+"F2.wireOp",EDGE,"E166.trimOffspring");Q29=makeQuery(id+"F2.imprint","IMPRINT",FACE,{"disambiguationData":[TD([[makeQuery(id+"F2.imprint","IMPRINT",EDGE,{"derivedFrom":subQ0}),-1.0]])]});}
            var Q30;
            {var subQ2=sQuery(id+"F2.wireOp",EDGE,"E163.trimOffspring");Q30=makeQuery(id+"F2.imprint","IMPRINT",FACE,{"disambiguationData":[TD([[makeQuery(id+"F2.imprint","IMPRINT",EDGE,{"derivedFrom":subQ2}),1.0]])]});}
            var Q31;
            {var subQ2=sQuery(id+"F2.wireOp",EDGE,"E162.trimOffspring");Q31=makeQuery(id+"F2.imprint","IMPRINT",FACE,{"disambiguationData":[TD([[makeQuery(id+"F2.imprint","IMPRINT",EDGE,{"derivedFrom":subQ2}),1.0]])]});}
            extrude(context, id + "F6", {"entities" : qUnion([Q0, Q1, Q2, Q3, Q4, Q5, Q6, Q7, Q8, Q9, Q10, Q11, Q12, Q13, Q14, Q15, Q16, Q17, Q18, Q19, Q20, Q21, Q22, Q23, Q24, Q25, Q26, Q27, Q28, Q29, Q30, Q31]), "operationType" : NewBodyOperationType.REMOVE, "depth" : 3.9 * mm});
        }
        {
            var Q0;
            {var subQ2=sQuery(id+"F2.wireOp",EDGE,"E192.trimOffspring");Q0=makeQuery(id+"F2.imprint","IMPRINT",FACE,{"disambiguationData":[TD([[makeQuery(id+"F2.imprint","IMPRINT",EDGE,{"derivedFrom":subQ2}),1.0]])]});}
            var Q1;
            {var subQ2=sQuery(id+"F2.wireOp",EDGE,"E97");Q1=makeQuery(id+"F2.imprint","IMPRINT",FACE,{"disambiguationData":[TD([[makeQuery(id+"F2.imprint","IMPRINT",EDGE,{"derivedFrom":subQ2}),1.0]])]});}
            var Q2;
            {var subQ0=sQuery(id+"F2.wireOp",EDGE,"E190.trimOffspring");Q2=makeQuery(id+"F2.imprint","IMPRINT",FACE,{"disambiguationData":[TD([[makeQuery(id+"F2.imprint","IMPRINT",EDGE,{"derivedFrom":subQ0}),-1.0]])]});}
            var Q3;
            Q3=makeQuery(id+"F2.imprint","IMPRINT",FACE,{"disambiguationData":[TD([[makeQuery(id+"F2.imprint","IMPRINT",EDGE,{"derivedFrom":sQuery(id+"F2.wireOp",EDGE,"E101")}),1.0]])]});
            var Q4;
            {var subQ2=sQuery(id+"F2.wireOp",EDGE,"E137");Q4=makeQuery(id+"F2.imprint","IMPRINT",FACE,{"disambiguationData":[TD([[makeQuery(id+"F2.imprint","IMPRINT",EDGE,{"derivedFrom":subQ2}),1.0]])]});}
            var Q5;
            {var subQ0=sQuery(id+"F2.wireOp",EDGE,"E182.trimOffspring");Q5=makeQuery(id+"F2.imprint","IMPRINT",FACE,{"disambiguationData":[TD([[makeQuery(id+"F2.imprint","IMPRINT",EDGE,{"derivedFrom":subQ0}),-1.0]])]});}
            var Q6;
            {var subQ0=sQuery(id+"F2.wireOp",EDGE,"E170.trimOffspring");Q6=makeQuery(id+"F2.imprint","IMPRINT",FACE,{"disambiguationData":[TD([[makeQuery(id+"F2.imprint","IMPRINT",EDGE,{"derivedFrom":subQ0}),-1.0]])]});}
            var Q7;
            {var subQ0=sQuery(id+"F2.wireOp",EDGE,"E115");Q7=makeQuery(id+"F2.imprint","IMPRINT",FACE,{"disambiguationData":[TD([[makeQuery(id+"F2.imprint","IMPRINT",EDGE,{"derivedFrom":subQ0}),1.0]])]});}
            var Q8;
            {var subQ0=sQuery(id+"F2.wireOp",EDGE,"E116");Q8=makeQuery(id+"F2.imprint","IMPRINT",FACE,{"disambiguationData":[TD([[makeQuery(id+"F2.imprint","IMPRINT",EDGE,{"derivedFrom":subQ0}),-1.0]])]});}
            var Q9;
            {var subQ0=sQuery(id+"F2.wireOp",EDGE,"E117");Q9=makeQuery(id+"F2.imprint","IMPRINT",FACE,{"disambiguationData":[TD([[makeQuery(id+"F2.imprint","IMPRINT",EDGE,{"derivedFrom":subQ0}),1.0]])]});}
            var Q10;
            {var subQ0=sQuery(id+"F2.wireOp",EDGE,"E119");Q10=makeQuery(id+"F2.imprint","IMPRINT",FACE,{"disambiguationData":[TD([[makeQuery(id+"F2.imprint","IMPRINT",EDGE,{"derivedFrom":subQ0}),1.0]])]});}
            var Q11;
            {var subQ0=sQuery(id+"F2.wireOp",EDGE,"E121");Q11=makeQuery(id+"F2.imprint","IMPRINT",FACE,{"disambiguationData":[TD([[makeQuery(id+"F2.imprint","IMPRINT",EDGE,{"derivedFrom":subQ0}),1.0]])]});}
            var Q12;
            {var subQ0=sQuery(id+"F2.wireOp",EDGE,"E123");Q12=makeQuery(id+"F2.imprint","IMPRINT",FACE,{"disambiguationData":[TD([[makeQuery(id+"F2.imprint","IMPRINT",EDGE,{"derivedFrom":subQ0}),1.0]])]});}
            var Q13;
            {var subQ0=sQuery(id+"F2.wireOp",EDGE,"E125");Q13=makeQuery(id+"F2.imprint","IMPRINT",FACE,{"disambiguationData":[TD([[makeQuery(id+"F2.imprint","IMPRINT",EDGE,{"derivedFrom":subQ0}),1.0]])]});}
            var Q14;
            {var subQ0=sQuery(id+"F2.wireOp",EDGE,"E127");Q14=makeQuery(id+"F2.imprint","IMPRINT",FACE,{"disambiguationData":[TD([[makeQuery(id+"F2.imprint","IMPRINT",EDGE,{"derivedFrom":subQ0}),1.0]])]});}
            var Q15;
            {var subQ0=sQuery(id+"F2.wireOp",EDGE,"E129");Q15=makeQuery(id+"F2.imprint","IMPRINT",FACE,{"disambiguationData":[TD([[makeQuery(id+"F2.imprint","IMPRINT",EDGE,{"derivedFrom":subQ0}),1.0]])]});}
            var Q16;
            {var subQ0=sQuery(id+"F2.wireOp",EDGE,"E131");Q16=makeQuery(id+"F2.imprint","IMPRINT",FACE,{"disambiguationData":[TD([[makeQuery(id+"F2.imprint","IMPRINT",EDGE,{"derivedFrom":subQ0}),1.0]])]});}
            var Q17;
            {var subQ0=sQuery(id+"F2.wireOp",EDGE,"E133");Q17=makeQuery(id+"F2.imprint","IMPRINT",FACE,{"disambiguationData":[TD([[makeQuery(id+"F2.imprint","IMPRINT",EDGE,{"derivedFrom":subQ0}),1.0]])]});}
            var Q18;
            {var subQ0=sQuery(id+"F2.wireOp",EDGE,"E135");Q18=makeQuery(id+"F2.imprint","IMPRINT",FACE,{"disambiguationData":[TD([[makeQuery(id+"F2.imprint","IMPRINT",EDGE,{"derivedFrom":subQ0}),1.0]])]});}
            var Q19;
            {var subQ0=sQuery(id+"F2.wireOp",EDGE,"E139");Q19=makeQuery(id+"F2.imprint","IMPRINT",FACE,{"disambiguationData":[TD([[makeQuery(id+"F2.imprint","IMPRINT",EDGE,{"derivedFrom":subQ0}),1.0]])]});}
            var Q20;
            {var subQ0=sQuery(id+"F2.wireOp",EDGE,"E141");Q20=makeQuery(id+"F2.imprint","IMPRINT",FACE,{"disambiguationData":[TD([[makeQuery(id+"F2.imprint","IMPRINT",EDGE,{"derivedFrom":subQ0}),1.0]])]});}
            var Q21;
            {var subQ0=sQuery(id+"F2.wireOp",EDGE,"E143");Q21=makeQuery(id+"F2.imprint","IMPRINT",FACE,{"disambiguationData":[TD([[makeQuery(id+"F2.imprint","IMPRINT",EDGE,{"derivedFrom":subQ0}),1.0]])]});}
            var Q22;
            {var subQ2=sQuery(id+"F2.wireOp",EDGE,"E188.trimOffspring");Q22=makeQuery(id+"F2.imprint","IMPRINT",FACE,{"disambiguationData":[TD([[makeQuery(id+"F2.imprint","IMPRINT",EDGE,{"derivedFrom":subQ2}),1.0]])]});}
            var Q23;
            {var subQ0=sQuery(id+"F2.wireOp",EDGE,"E186.trimOffspring");Q23=makeQuery(id+"F2.imprint","IMPRINT",FACE,{"disambiguationData":[TD([[makeQuery(id+"F2.imprint","IMPRINT",EDGE,{"derivedFrom":subQ0}),-1.0]])]});}
            var Q24;
            {var subQ2=sQuery(id+"F2.wireOp",EDGE,"E180.trimOffspring");Q24=makeQuery(id+"F2.imprint","IMPRINT",FACE,{"disambiguationData":[TD([[makeQuery(id+"F2.imprint","IMPRINT",EDGE,{"derivedFrom":subQ2}),1.0]])]});}
            var Q25;
            {var subQ2=sQuery(id+"F2.wireOp",EDGE,"E178.trimOffspring");Q25=makeQuery(id+"F2.imprint","IMPRINT",FACE,{"disambiguationData":[TD([[makeQuery(id+"F2.imprint","IMPRINT",EDGE,{"derivedFrom":subQ2}),1.0]])]});}
            var Q26;
            {var subQ0=sQuery(id+"F2.wireOp",EDGE,"E176.trimOffspring");Q26=makeQuery(id+"F2.imprint","IMPRINT",FACE,{"disambiguationData":[TD([[makeQuery(id+"F2.imprint","IMPRINT",EDGE,{"derivedFrom":subQ0}),-1.0]])]});}
            var Q27;
            {var subQ2=sQuery(id+"F2.wireOp",EDGE,"E172.trimOffspring");Q27=makeQuery(id+"F2.imprint","IMPRINT",FACE,{"disambiguationData":[TD([[makeQuery(id+"F2.imprint","IMPRINT",EDGE,{"derivedFrom":subQ2}),1.0]])]});}
            var Q28;
            {var subQ0=sQuery(id+"F2.wireOp",EDGE,"E168.trimOffspring");Q28=makeQuery(id+"F2.imprint","IMPRINT",FACE,{"disambiguationData":[TD([[makeQuery(id+"F2.imprint","IMPRINT",EDGE,{"derivedFrom":subQ0}),-1.0]])]});}
            var Q29;
            {var subQ0=sQuery(id+"F2.wireOp",EDGE,"E166.trimOffspring");Q29=makeQuery(id+"F2.imprint","IMPRINT",FACE,{"disambiguationData":[TD([[makeQuery(id+"F2.imprint","IMPRINT",EDGE,{"derivedFrom":subQ0}),-1.0]])]});}
            var Q30;
            {var subQ2=sQuery(id+"F2.wireOp",EDGE,"E163.trimOffspring");Q30=makeQuery(id+"F2.imprint","IMPRINT",FACE,{"disambiguationData":[TD([[makeQuery(id+"F2.imprint","IMPRINT",EDGE,{"derivedFrom":subQ2}),1.0]])]});}
            var Q31;
            {var subQ2=sQuery(id+"F2.wireOp",EDGE,"E162.trimOffspring");Q31=makeQuery(id+"F2.imprint","IMPRINT",FACE,{"disambiguationData":[TD([[makeQuery(id+"F2.imprint","IMPRINT",EDGE,{"derivedFrom":subQ2}),1.0]])]});}
            extrude(context, id + "F7", {"entities" : qUnion([Q0, Q1, Q2, Q3, Q4, Q5, Q6, Q7, Q8, Q9, Q10, Q11, Q12, Q13, Q14, Q15, Q16, Q17, Q18, Q19, Q20, Q21, Q22, Q23, Q24, Q25, Q26, Q27, Q28, Q29, Q30, Q31]), "depth" : 2.3 * mm});
        }
        {
            var Q0;
            Q0=makeQuery(id+"F3.opExtrude","SWEPT_BODY",BODY,{"disambiguationData":[OSD([sQuery(id+"F0.wireOp",EDGE,"E0.left"),sQuery(id+"F0.wireOp",EDGE,"E0.right"),sQuery(id+"F0.wireOp",EDGE,"E1.left"),sQuery(id+"F0.wireOp",EDGE,"E2"),sQuery(id+"F0.wireOp",EDGE,"E3"),sQuery(id+"F0.wireOp",EDGE,"E4"),sQuery(id+"F0.wireOp",EDGE,"E5"),sQuery(id+"F0.wireOp",EDGE,"E6"),sQuery(id+"F0.wireOp",EDGE,"E7"),sQuery(id+"F0.wireOp",EDGE,"E8"),sQuery(id+"F0.wireOp",EDGE,"E9"),sQuery(id+"F0.wireOp",EDGE,"E10"),sQuery(id+"F0.wireOp",EDGE,"E12"),sQuery(id+"F0.wireOp",EDGE,"E14"),sQuery(id+"F0.wireOp",EDGE,"E15")])]});
            transform(context, id + "F8", {"entities" : qUnion([Q0]), "transformType" : TransformType.TRANSLATION_3D, "dx" : 0 * mm, "dy" : 0 * mm, "dz" : 0 * mm, "makeCopy" : true});
        }
    });
